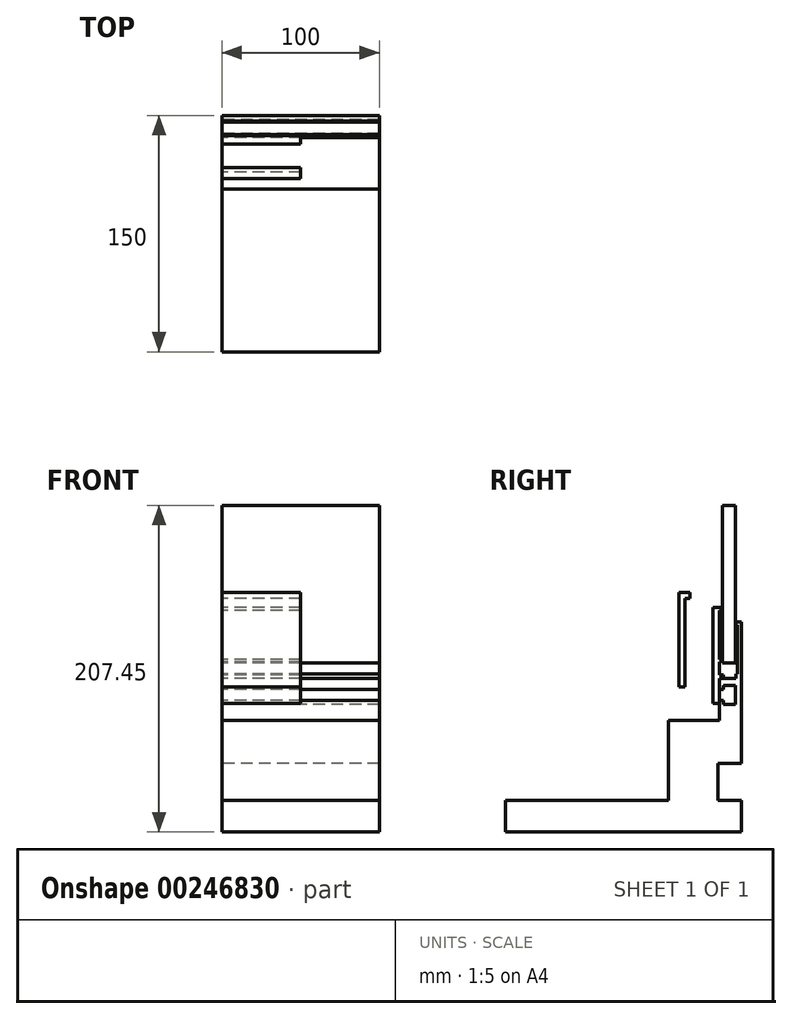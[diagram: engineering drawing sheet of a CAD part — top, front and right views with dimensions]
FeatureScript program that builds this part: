
annotation { "Feature Type Name" : "Feature", "Feature Type Description" : "" }
export const myFeature = defineFeature(function(context is Context, id is Id, definition is map)
    precondition{}
    {
        {
            var Q0;
            Q0=qCreatedBy(makeId("Right.planeOp"),FACE);
            var sketch = newSketch(context, id + "F0", { "sketchPlane" : qUnion([Q0])});
            skLineSegment(sketch, "E0", {"start": v(0, 133.45) * mm, "end": v(0, 43.45) * mm});
            skLineSegment(sketch, "E1", {"start": v(0, 43.45) * mm, "end": v(-15, 43.45) * mm});
            skLineSegment(sketch, "E2", {"start": v(-15, 43.45) * mm, "end": v(-15, 20) * mm});
            skLineSegment(sketch, "E3", {"start": v(-15, 20) * mm, "end": v(0, 20) * mm});
            skLineSegment(sketch, "E4", {"start": v(0, 20) * mm, "end": v(0, 0) * mm});
            skLineSegment(sketch, "E5", {"start": v(0, 0) * mm, "end": v(-150, 0) * mm});
            skLineSegment(sketch, "E6", {"start": v(-150, 0) * mm, "end": v(-150, 20) * mm});
            skLineSegment(sketch, "E7", {"start": v(-150, 20) * mm, "end": v(-46.54, 20) * mm});
            skLineSegment(sketch, "E8", {"start": v(-46.54, 20) * mm, "end": v(-46.54, 70.75) * mm});
            skLineSegment(sketch, "E9", {"start": v(-46.54, 70.75) * mm, "end": v(-14, 70.75) * mm});
            skLineSegment(sketch, "E10", {"start": v(-14, 70.75) * mm, "end": v(-14, 83.45) * mm});
            skLineSegment(sketch, "E11", {"start": v(-14, 83.45) * mm, "end": v(-11.5, 83.45) * mm});
            skLineSegment(sketch, "E12", {"start": v(-11.5, 83.45) * mm, "end": v(-11.5, 80.95) * mm});
            skLineSegment(sketch, "E13", {"start": v(-11.5, 80.95) * mm, "end": v(-4, 80.95) * mm});
            skLineSegment(sketch, "E14", {"start": v(-4, 80.95) * mm, "end": v(-4, 92.95) * mm});
            skLineSegment(sketch, "E15", {"start": v(-4, 92.95) * mm, "end": v(-11.5, 92.95) * mm});
            skLineSegment(sketch, "E16", {"start": v(-11.5, 92.95) * mm, "end": v(-11.5, 90.45) * mm});
            skLineSegment(sketch, "E17", {"start": v(-11.5, 90.45) * mm, "end": v(-14, 90.45) * mm});
            skLineSegment(sketch, "E18", {"start": v(-14, 90.45) * mm, "end": v(-14, 97.45) * mm});
            skLineSegment(sketch, "E19", {"start": v(-14, 97.45) * mm, "end": v(-3.5, 97.45) * mm});
            skLineSegment(sketch, "E20", {"start": v(-3.5, 97.45) * mm, "end": v(-3.5, 100.45) * mm});
            skLineSegment(sketch, "E21", {"start": v(-3.5, 100.45) * mm, "end": v(-2.5, 100.45) * mm});
            skLineSegment(sketch, "E22", {"start": v(-2.5, 100.45) * mm, "end": v(-2.5, 131.45) * mm});
            skLineSegment(sketch, "E23", {"start": v(-2.5, 131.45) * mm, "end": v(-3.5, 131.45) * mm});
            skLineSegment(sketch, "E24", {"start": v(-3.5, 131.45) * mm, "end": v(-3.5, 133.45) * mm});
            skLineSegment(sketch, "E25", {"start": v(-3.5, 133.45) * mm, "end": v(0, 133.45) * mm});
            skSolve(sketch);
        }
        {
            var Q0;
            Q0=makeQuery(id+"F0.imprint","IMPRINT",FACE,{"disambiguationData":[TD([[makeQuery(id+"F0.imprint","IMPRINT",EDGE,{"derivedFrom":sQuery(id+"F0.wireOp",EDGE,"E0")}),-1.0]])]});
            extrude(context, id + "F1", {"entities" : qUnion([Q0]), "depth" : 100 * mm});
        }
        {
            var Q0;
            Q0=qCreatedBy(makeId("Right.planeOp"),FACE);
            var sketch = newSketch(context, id + "F2", { "sketchPlane" : qUnion([Q0])});
            skLineSegment(sketch, "E26.bottom", {"start": v(-4, 107.45) * mm, "end": v(-12, 107.45) * mm});
            skLineSegment(sketch, "E26.top", {"start": v(-4, 207.45) * mm, "end": v(-12, 207.45) * mm});
            skLineSegment(sketch, "E26.left", {"start": v(-4, 107.45) * mm, "end": v(-4, 207.45) * mm});
            skLineSegment(sketch, "E26.right", {"start": v(-12, 107.45) * mm, "end": v(-12, 207.45) * mm});
            skSolve(sketch);
        }
        {
            var Q0;
            Q0=makeQuery(id+"F2.imprint","IMPRINT",FACE,{"disambiguationData":[TD([[makeQuery(id+"F2.imprint","IMPRINT",EDGE,{"derivedFrom":sQuery(id+"F2.wireOp",EDGE,"E26.bottom")}),-1.0]])]});
            extrude(context, id + "F3", {"entities" : qUnion([Q0]), "depth" : 100 * mm});
        }
        {
            var Q0;
            Q0=qCreatedBy(makeId("Right.planeOp"),FACE);
            var sketch = newSketch(context, id + "F4", { "sketchPlane" : qUnion([Q0])});
            skLineSegment(sketch, "E27", {"start": v(-12.6, 142.55) * mm, "end": v(-18.1, 142.55) * mm});
            skLineSegment(sketch, "E28", {"start": v(-18.1, 142.55) * mm, "end": v(-18.1, 81.55) * mm});
            skLineSegment(sketch, "E29", {"start": v(-18.1, 81.55) * mm, "end": v(-14.1, 81.55) * mm});
            skLineSegment(sketch, "E30", {"start": v(-14.1, 81.55) * mm, "end": v(-14.1, 97.55) * mm});
            skLineSegment(sketch, "E31", {"start": v(-14.1, 97.55) * mm, "end": v(-11.6, 97.55) * mm});
            skLineSegment(sketch, "E32", {"start": v(-11.6, 97.55) * mm, "end": v(-11.6, 99.55) * mm});
            skLineSegment(sketch, "E33", {"start": v(-11.6, 99.55) * mm, "end": v(-14.1, 99.55) * mm});
            skLineSegment(sketch, "E34", {"start": v(-14.1, 99.55) * mm, "end": v(-14.1, 108.05) * mm});
            skLineSegment(sketch, "E35", {"start": v(-14.1, 108.05) * mm, "end": v(-13.1, 108.05) * mm});
            skLineSegment(sketch, "E36", {"start": v(-13.1, 108.05) * mm, "end": v(-13.1, 109.55) * mm});
            skLineSegment(sketch, "E37", {"start": v(-13.1, 109.55) * mm, "end": v(-14.1, 109.55) * mm});
            skLineSegment(sketch, "E38", {"start": v(-14.1, 109.55) * mm, "end": v(-14.1, 140.55) * mm});
            skLineSegment(sketch, "E39", {"start": v(-14.1, 140.55) * mm, "end": v(-12.6, 140.55) * mm});
            skLineSegment(sketch, "E40", {"start": v(-12.6, 140.55) * mm, "end": v(-12.6, 142.55) * mm});
            skSolve(sketch);
        }
        {
            var Q0;
            Q0 = qSketchRegion(id + "F4", true);
            extrude(context, id + "F5", {"entities" : qUnion([Q0]), "depth" : 50 * mm});
        }
        {
            var Q0;
            Q0=qCreatedBy(makeId("Right.planeOp"),FACE);
            var sketch = newSketch(context, id + "F6", { "sketchPlane" : qUnion([Q0])});
            skLineSegment(sketch, "E41", {"start": v(-35.86, 92.17) * mm, "end": v(-35.86, 148.17) * mm});
            skLineSegment(sketch, "E42", {"start": v(-35.86, 148.17) * mm, "end": v(-32.86, 148.17) * mm});
            skLineSegment(sketch, "E43", {"start": v(-32.86, 148.17) * mm, "end": v(-32.86, 152.17) * mm});
            skLineSegment(sketch, "E44", {"start": v(-32.86, 152.17) * mm, "end": v(-39.86, 152.17) * mm});
            skLineSegment(sketch, "E45", {"start": v(-39.86, 152.17) * mm, "end": v(-39.86, 92.17) * mm});
            skLineSegment(sketch, "E46", {"start": v(-39.86, 92.17) * mm, "end": v(-35.86, 92.17) * mm});
            skSolve(sketch);
        }
        {
            var Q0;
            Q0 = qSketchRegion(id + "F6", true);
            extrude(context, id + "F7", {"entities" : qUnion([Q0]), "depth" : 50 * mm});
        }
    });
